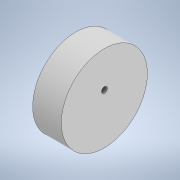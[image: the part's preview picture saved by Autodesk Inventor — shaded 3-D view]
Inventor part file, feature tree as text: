
AUTODESK INVENTOR PART (.ipt)
format: ipt  version: 2022 (Build 260153000, 153)  size: 128,512 bytes
history: native  units: mm
features: sketch x3, revolve x2, other x1, extrude x1, projected_geometry x1
ambient origin geometry x8: Origin, YZ Plane, XZ Plane, XY Plane, X Axis, Y Axis, Z Axis, Center Point
bodies: Body1 (feature_tree)
feature tree (8):
  other  "Твердое тело1"
  revolve  "Вращение1"
  extrude  "Выдавливание1"  Depth=20.0mm
  revolve  "Вращение3"
  sketch  "Эскиз1"
  sketch  "Эскиз2"
  sketch  "Эскиз3"
  projected_geometry  "Спроецированная петля1"
